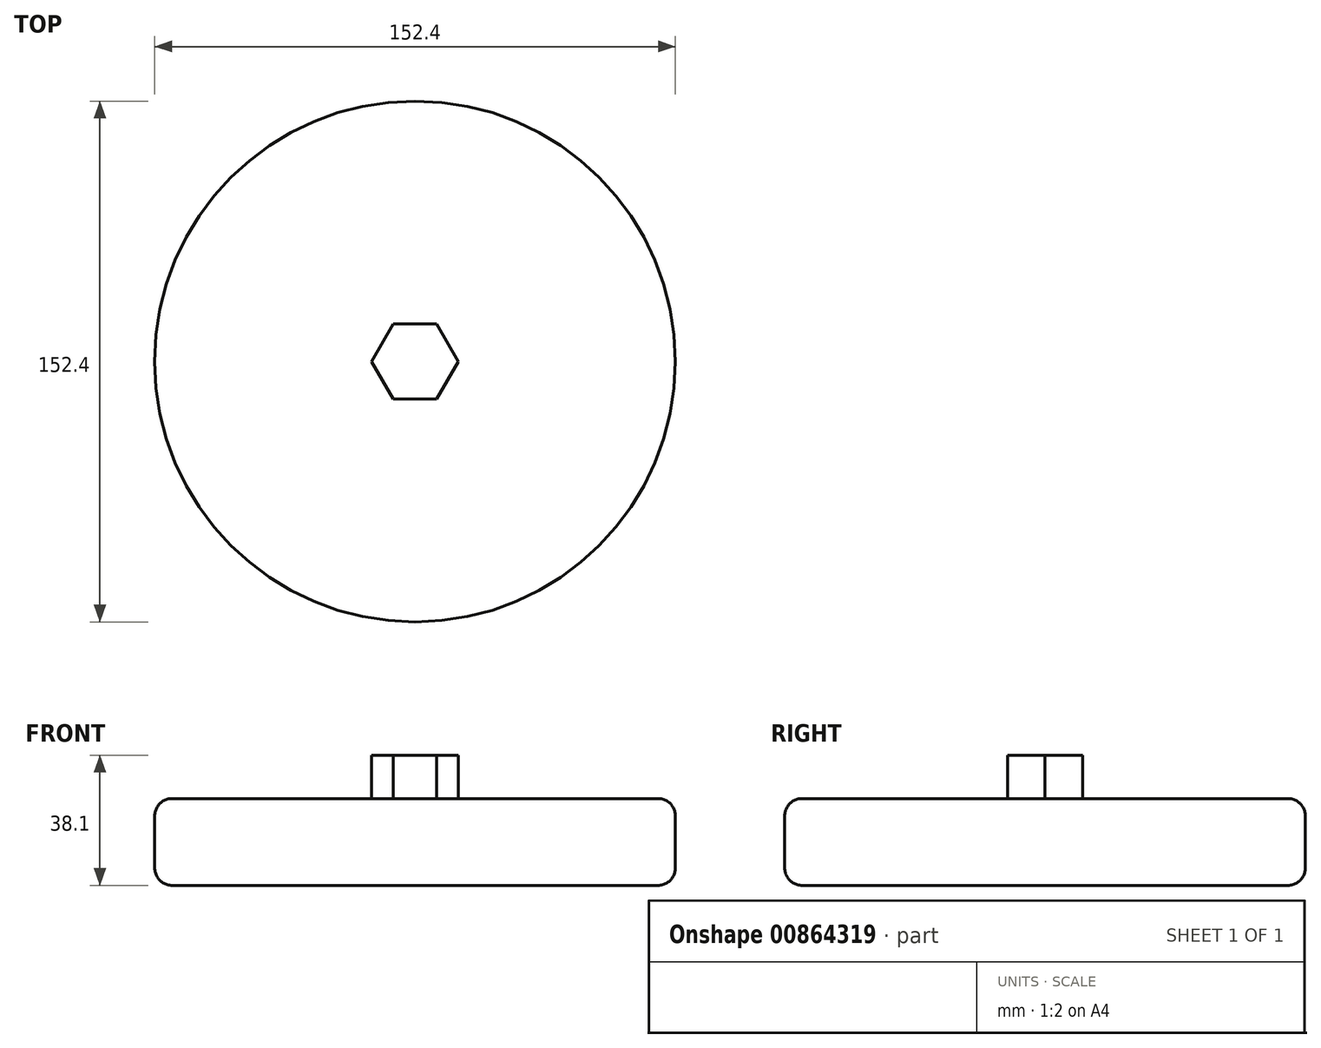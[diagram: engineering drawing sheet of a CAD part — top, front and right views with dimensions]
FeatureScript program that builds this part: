
annotation { "Feature Type Name" : "Feature", "Feature Type Description" : "" }
export const myFeature = defineFeature(function(context is Context, id is Id, definition is map)
    precondition{}
    {
        {
            var Q0;
            Q0=qCreatedBy(makeId("Top.planeOp"),FACE);
            var sketch = newSketch(context, id + "F0", { "sketchPlane" : qUnion([Q0])});
            skCircle(sketch, "E0", {"center": v(0, 0) * mm, "radius": 76.2 * mm});
            skSolve(sketch);
        }
        {
            var Q0;
            Q0=makeQuery(id+"F0.imprint","IMPRINT",FACE,{"disambiguationData":[TD([[makeQuery(id+"F0.imprint","IMPRINT",EDGE,{"derivedFrom":sQuery(id+"F0.wireOp",EDGE,"E0")}),1.0]])]});
            extrude(context, id + "F1", {"entities" : qUnion([Q0]), "depth" : 25.4 * mm, "offsetDistance" : 25.4 * mm});
        }
        {
            var Q0;
            Q0=makeQuery(id+"F1.opExtrude","CAP_EDGE",EDGE,{"disambiguationData":[OSD([sQuery(id+"F0.wireOp",EDGE,"E0")])],"isStart":false});
            var Q1;
            Q1=makeQuery(id+"F1.opExtrude","CAP_EDGE",EDGE,{"disambiguationData":[OSD([sQuery(id+"F0.wireOp",EDGE,"E0")])],"isStart":true});
            fillet(context, id + "F2", {"entities" : qUnion([Q0, Q1]), "radius" : 5.08 * mm, "tangentPropagation" : true, "allowEdgeOverflow" : false});
        }
        {
            var Q0;
            Q0=makeQuery(id+"F1.opExtrude","CAP_FACE",FACE,{"disambiguationData":[OSD([sQuery(id+"F0.wireOp",EDGE,"E0")])],"isStart":false});
            var sketch = newSketch(context, id + "F3", { "sketchPlane" : qUnion([Q0])});
            skCircle(sketch, "E1.cCircle", {"center": v(0, 0) * mm, "radius": 12.7 * mm, "construction": true});
            skLineSegment(sketch, "E1.0", {"start": v(6.35, -11) * mm, "end": v(-6.35, -11) * mm});
            skLineSegment(sketch, "E1.1", {"start": v(-6.35, -11) * mm, "end": v(-12.7, 0) * mm});
            skLineSegment(sketch, "E1.2", {"start": v(-12.7, 0) * mm, "end": v(-6.35, 11) * mm});
            skLineSegment(sketch, "E1.3", {"start": v(-6.35, 11) * mm, "end": v(6.35, 11) * mm});
            skLineSegment(sketch, "E1.4", {"start": v(6.35, 11) * mm, "end": v(12.7, 0) * mm});
            skLineSegment(sketch, "E1.5", {"start": v(12.7, 0) * mm, "end": v(6.35, -11) * mm});
            skSolve(sketch);
        }
        {
            var Q0;
            Q0 = qSketchRegion(id + "F3", true);
            extrude(context, id + "F4", {"entities" : qUnion([Q0]), "operationType" : NewBodyOperationType.ADD, "depth" : 12.7 * mm, "offsetDistance" : 25.4 * mm});
        }
    });
